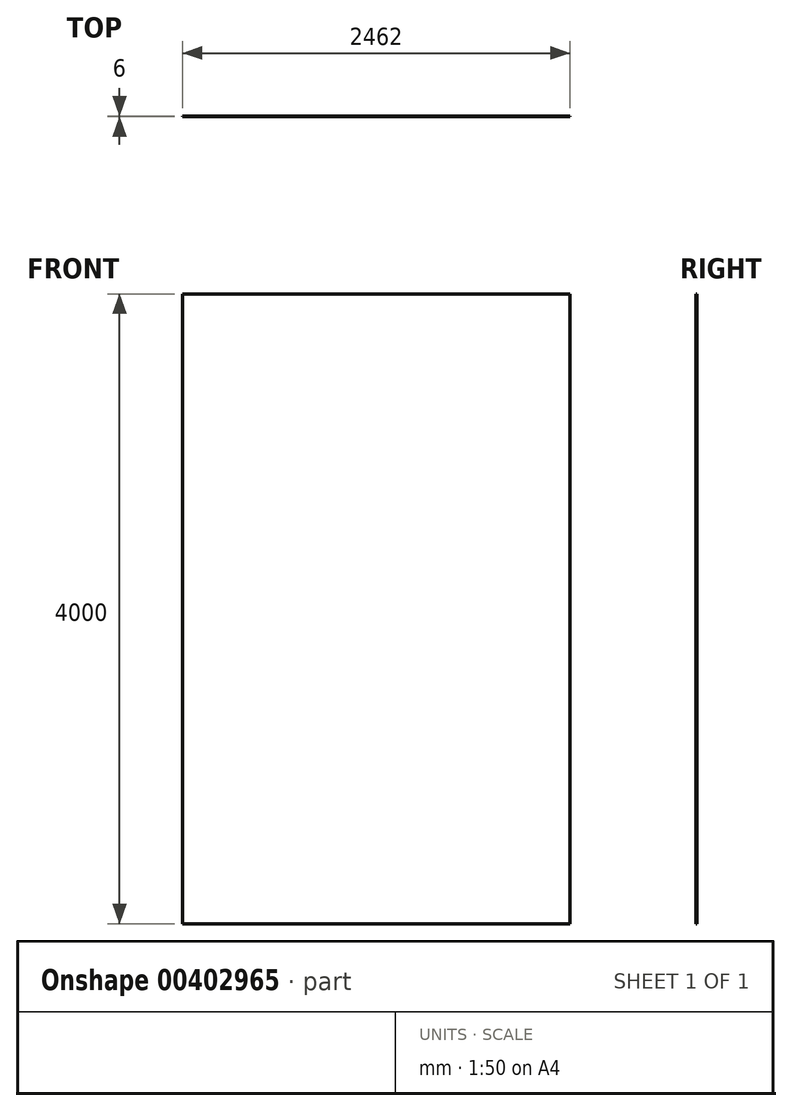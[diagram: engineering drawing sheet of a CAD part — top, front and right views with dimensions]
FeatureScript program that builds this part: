
annotation { "Feature Type Name" : "Feature", "Feature Type Description" : "" }
export const myFeature = defineFeature(function(context is Context, id is Id, definition is map)
    precondition{}
    {
        {
            var Q0;
            Q0=qCreatedBy(makeId("Front.planeOp"),FACE);
            var sketch = newSketch(context, id + "F0", { "sketchPlane" : qUnion([Q0])});
            skLineSegment(sketch, "E0.bottom", {"start": v(-1231, 2000) * mm, "end": v(1231, 2000) * mm});
            skLineSegment(sketch, "E0.top", {"start": v(-1231, -2000) * mm, "end": v(1231, -2000) * mm});
            skLineSegment(sketch, "E0.left", {"start": v(-1231, 2000) * mm, "end": v(-1231, -2000) * mm});
            skLineSegment(sketch, "E0.right", {"start": v(1231, 2000) * mm, "end": v(1231, -2000) * mm});
            skPoint(sketch, "E0.middle", {"position": v(0, 0) * mm});
            skSolve(sketch);
        }
        {
            var Q0;
            Q0=makeQuery(id+"F0.imprint","IMPRINT",FACE,{"disambiguationData":[TD([[makeQuery(id+"F0.imprint","IMPRINT",EDGE,{"derivedFrom":sQuery(id+"F0.wireOp",EDGE,"E0.bottom")}),-1.0]])]});
            extrude(context, id + "F1", {"entities" : qUnion([Q0]), "depth" : 6 * mm});
        }
    });
